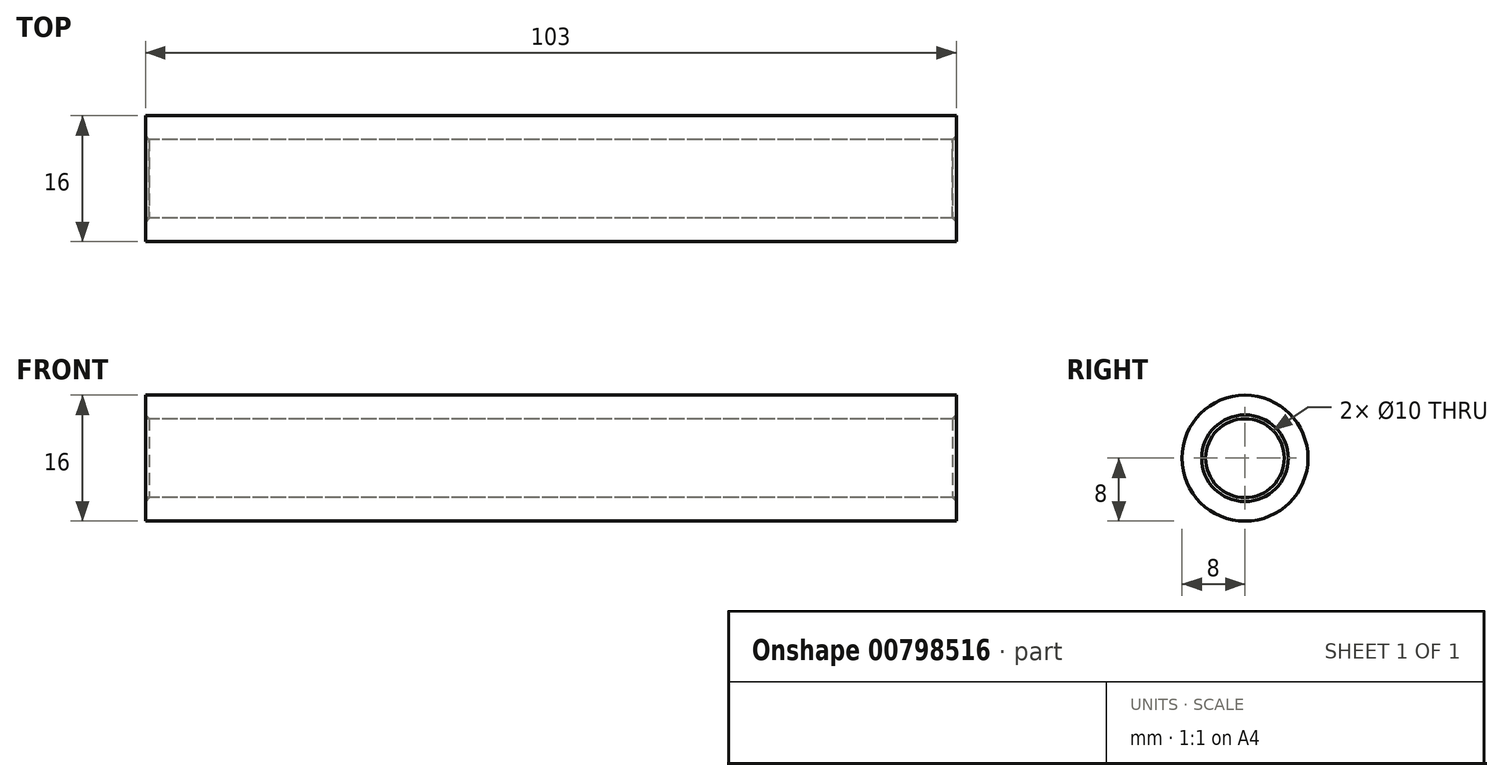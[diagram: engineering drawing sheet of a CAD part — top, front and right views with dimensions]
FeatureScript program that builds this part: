
annotation { "Feature Type Name" : "Feature", "Feature Type Description" : "" }
export const myFeature = defineFeature(function(context is Context, id is Id, definition is map)
    precondition{}
    {
        {
            var Q0;
            Q0=qCreatedBy(makeId("Front.planeOp"),FACE);
            var sketch = newSketch(context, id + "F0", { "sketchPlane" : qUnion([Q0])});
            skLineSegment(sketch, "E0.bottom", {"start": v(0, 5) * mm, "end": v(103, 5) * mm});
            skLineSegment(sketch, "E0.top", {"start": v(0, 8) * mm, "end": v(103, 8) * mm});
            skLineSegment(sketch, "E0.left", {"start": v(0, 5) * mm, "end": v(0, 8) * mm});
            skLineSegment(sketch, "E0.right", {"start": v(103, 5) * mm, "end": v(103, 8) * mm});
            skLineSegment(sketch, "E1", {"start": v(-65.27, 0) * mm, "end": v(125.2, 0) * mm, "construction": true});
            skLineSegment(sketch, "E2.MirrorCS", {"start": v(103, -5) * mm, "end": v(103, -8) * mm});
            skLineSegment(sketch, "E3.MirrorCS", {"start": v(0, -5) * mm, "end": v(0, -8) * mm});
            skLineSegment(sketch, "E4.MirrorCS", {"start": v(0, -5) * mm, "end": v(103, -5) * mm});
            skLineSegment(sketch, "E5.MirrorCS", {"start": v(0, -8) * mm, "end": v(103, -8) * mm});
            skSolve(sketch);
        }
        {
            var Q0;
            Q0 = qSketchRegion(id + "F0", true);
            var Q1;
            Q1=sQuery(id+"F0.wireOp",EDGE,"E1");
            revolve(context, id + "F1", {"surfaceOperationType" : NewSurfaceOperationType.NEW, "entities" : qUnion([Q0]), "axis" : qUnion([Q1]), "revolveType" : RevolveType.FULL});
        }
        {
            var Q0;
            Q0=makeQuery(id+"F1.opRevolve","SWEPT_EDGE",EDGE,{"disambiguationData":[OSD([sQuery(id+"F0.wireOp",EDGE,"E0.bottom"),sQuery(id+"F0.wireOp",EDGE,"E0.left")])]});
            var Q1;
            Q1=makeQuery(id+"F1.opRevolve","SWEPT_EDGE",EDGE,{"disambiguationData":[OSD([sQuery(id+"F0.wireOp",EDGE,"E0.bottom"),sQuery(id+"F0.wireOp",EDGE,"E0.right")])]});
            chamfer(context, id + "F2", {"entities" : qUnion([Q0, Q1]), "width" : 0.5 * mm, "tangentPropagation" : true});
        }
    });
